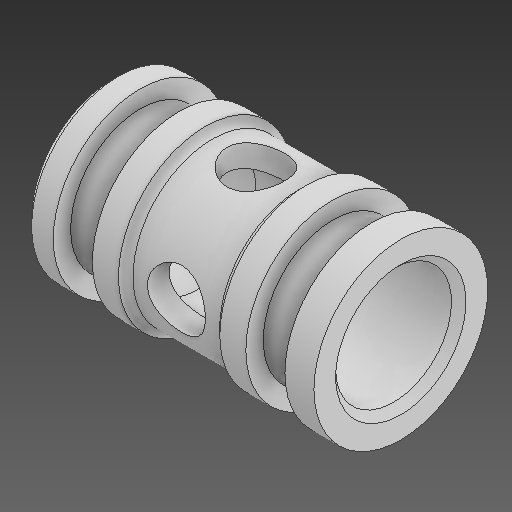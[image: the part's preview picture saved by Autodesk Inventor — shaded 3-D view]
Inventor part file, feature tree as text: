
AUTODESK INVENTOR PART (.ipt)
format: ipt  version: 2021 (Build 250183000, 183)  size: 240,128 bytes
history: native  units: in
note: dims shown in document units (in); Inventor stores cm internally (conversion verified against a paired STEP export)
features: other x3, sketch x2, plane x1
ambient origin geometry x8: Origin, YZ Plane, XZ Plane, XY Plane, X Axis, Y Axis, Z Axis, Center Point
bodies: Solid1 (feature_tree)
feature tree (6):
  other  "checkBallValve.ipt"
  other  "Solid1::checkBallValve.ipt"
  other  "TaggingFeature1"
  sketch  "Sketch2"  dims[d0=0.3937in]
  sketch  "Sketch3"
  plane  "Work Plane1"
